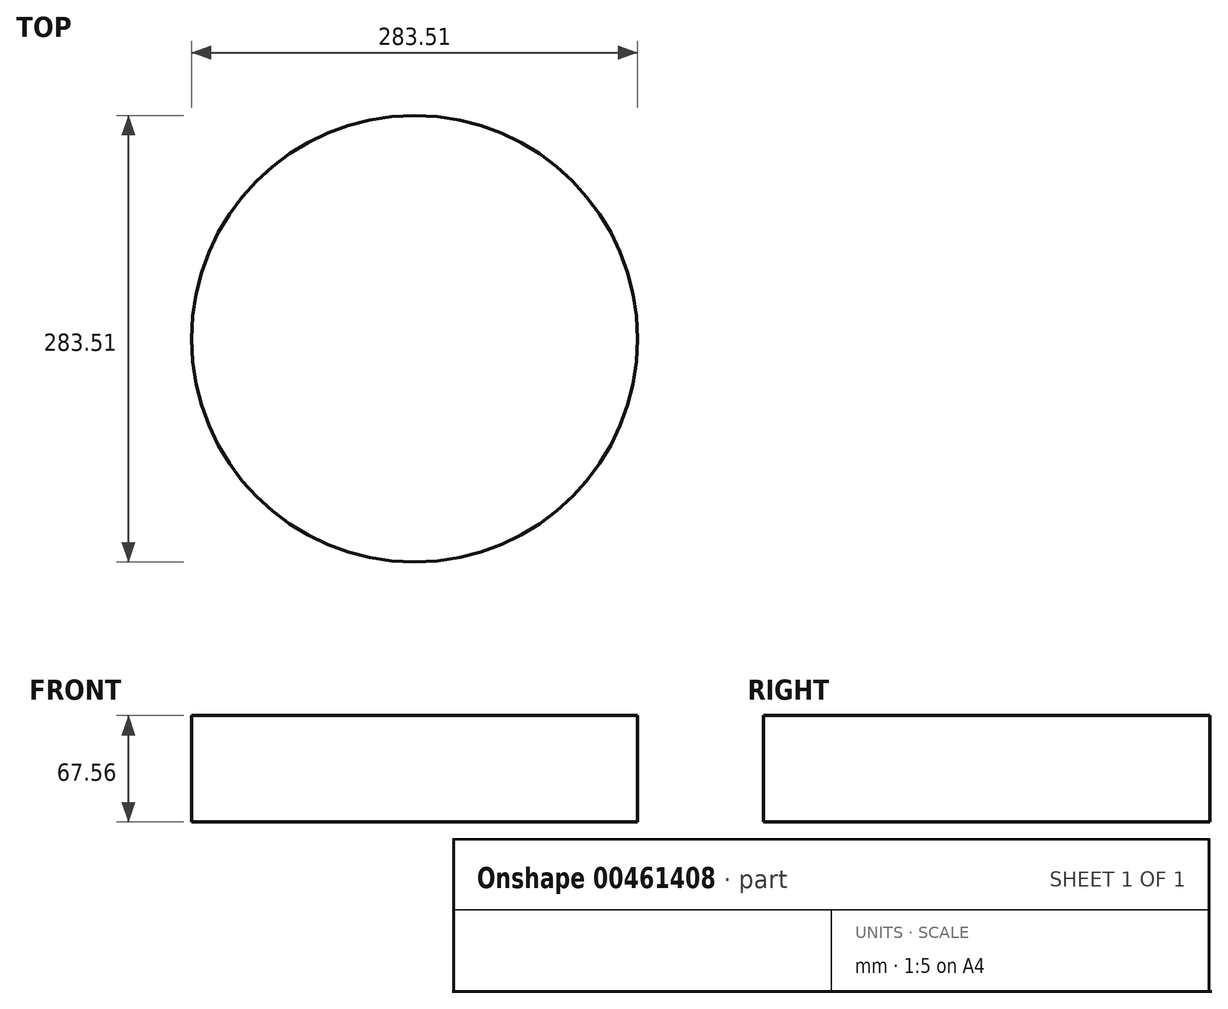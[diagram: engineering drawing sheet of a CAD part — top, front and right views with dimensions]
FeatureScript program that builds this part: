
annotation { "Feature Type Name" : "Feature", "Feature Type Description" : "" }
export const myFeature = defineFeature(function(context is Context, id is Id, definition is map)
    precondition{}
    {
        {
            var Q0;
            Q0=qCreatedBy(makeId("Top.planeOp"),FACE);
            var sketch = newSketch(context, id + "F0", { "sketchPlane" : qUnion([Q0])});
            skCircle(sketch, "E0", {"center": v(-77.14, -42.35) * mm, "radius": 141.75 * mm});
            skSolve(sketch);
        }
        {
            var Q0;
            Q0 = qSketchRegion(id + "F0", true);
            extrude(context, id + "F1", {"entities" : qUnion([Q0]), "depth" : 67.56 * mm});
        }
    });
